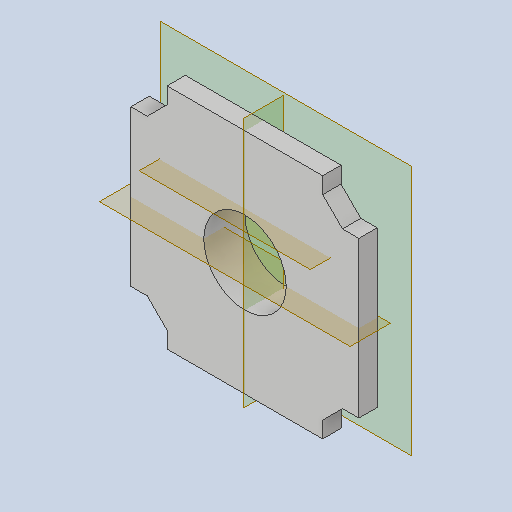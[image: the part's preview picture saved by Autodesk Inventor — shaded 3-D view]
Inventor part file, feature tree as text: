
AUTODESK INVENTOR PART (.ipt)
format: ipt  version: 2023 (Build 270158000, 158)  size: 797,696 bytes
history: native  units: mm
features: reference x17, other x11, sketch x8, extrude x7, plane x6, projected_geometry x3, pattern_circular x1
ambient origin geometry x8: Origin, YZ Plane, XZ Plane, XY Plane, X Axis, Y Axis, Z Axis, Center Point
bodies: Body1 (feature_tree)
feature tree (53):
  plane  "Work Plane1"
  extrude  "Extrusion1"  Depth=53.8mm
  extrude  "IM_offset"  Depth=53.8mm
  plane  "Arbeitsebene5"
  plane  "Arbeitsebene6"
  extrude  "Extrusion26"  Depth=45.0mm
  other  "Spirale2"
  sketch  "Skizze33"  dims[d32=2.8mm d33=2.8mm]
  plane  "Arbeitsebene9"
  extrude  "Extrusion27"  Depth=20.0mm
  plane  "Arbeitsebene10"
  extrude  "Extrusion28"  Depth=2.8mm
  plane  "Arbeitsebene11"
  extrude  "Extrusion29"  Depth=3.0mm
  pattern_circular  "Runde Anordnung1"  [2 undecoded]
  extrude  "Extrusion30"  Depth=4.0mm
  sketch  "Sketch1"  dims[d10=8.0mm d11=0.0mm d18=53.8mm]
  reference  "Reference1"
  reference  "Reference2"
  reference  "Reference3"
  reference  "Reference4"
  reference  "Reference9"
  reference  "Reference20"
  reference  "Reference21"
  reference  "Reference22"
  reference  "Reference23"
  reference  "Reference24"
  sketch  "Skizze4"  dims[d19=45.0deg d20=53.8mm]
  projected_geometry  "Projizierte Kontur1"
  sketch  "Skizze31"  dims[d21=45.0mm d22=45.0mm]
  projected_geometry  "Projizierte Kontur17"
  sketch  "Skizze32"  dims[d30=20.0mm d31=20.0mm]
  reference  "Referenz34"
  reference  "Referenz35"
  reference  "Referenz36"
  reference  "Referenz37"
  reference  "Referenz38"
  reference  "Referenz39"
  reference  "Referenz40"
  sketch  "Skizze34"  dims[d34=2.8mm d35=3.0mm]
  sketch  "Skizze35"  dims[d36=0.1mm]
  sketch  "Sketch36"  dims[d37=0.1mm d38=0.1mm d39=0.1mm d40=0.2mm d41=10.0mm d42=0.0mm d181=20.0mm d182=10.0mm d183=0.0mm d184=2.0mm d185=0.794438mm d186=0.794mm d187=10.0mm d188=80.0mm d189=0.0mm d190=90.0deg d191=90.0deg d192=0.0mm d193=0.0mm d194=18.0mm d195=5.0mm d196=0.0mm d197=5.0mm d198=3.0mm d199=0.0mm d200=-14.7mm d201=16.078963mm d202=3.0mm d203=0.0mm d204=30.0mm d205=360.0deg d207=4.0mm d208=0.0mm d209=8.0mm d210=0.0mm d160=0.5mm d161=0.872665mm d162=0.5mm d163=0.872665mm]
  projected_geometry  "Projected Loop18"
  other  "Assembly_Cube_v2_Thorlabs.iam"
  other  "10_Cube_Base:1"
  other  "00_Base_v0:1"
  other  "Assembly_Cube_Kinematic_Mirrormount_v2.iam"
  other  "Assembly_Cube_empty_1x1_v2:1"
  other  "10_Cube_1x1_v2:1"
  other  "10_Lid_1x1_v2:1"
  other  "Baugruppe1"
  other  "00_Cmount_Thread:1"
  other  "10_Cube_Lid:1"
note: 2 required parameter values undecoded (feature->parameter linkage not recoverable at this tier; creation-order binding heuristic only, values carry confidence <= 0.55)
